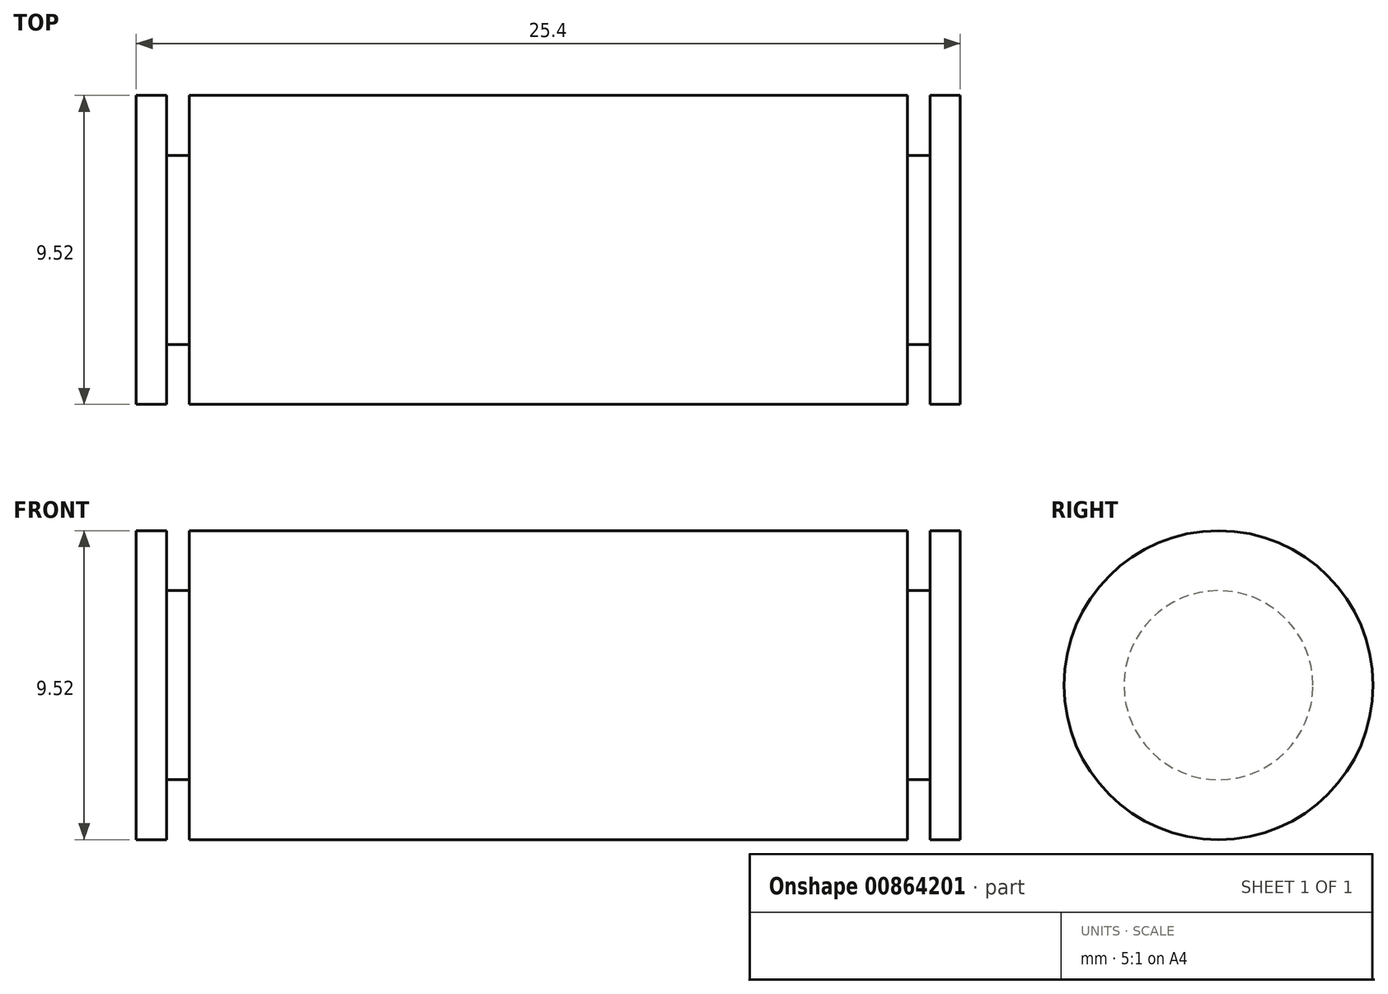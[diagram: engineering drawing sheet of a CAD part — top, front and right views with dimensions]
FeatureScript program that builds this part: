
annotation { "Feature Type Name" : "Feature", "Feature Type Description" : "" }
export const myFeature = defineFeature(function(context is Context, id is Id, definition is map)
    precondition{}
    {
        {
            var Q0;
            Q0=qCreatedBy(makeId("Right.planeOp"),FACE);
            var sketch = newSketch(context, id + "F0", { "sketchPlane" : qUnion([Q0])});
            skCircle(sketch, "E0", {"center": v(0, 0) * mm, "radius": 4.76 * mm});
            skSolve(sketch);
        }
        {
            var Q0;
            Q0=qSketchRegion(id+"F0",true);
            extrude(context, id + "F1", {"entities" : qUnion([Q0]), "depth" : 12.7 * mm, "offsetDistance" : 25.4 * mm});
        }
        {
            var Q0;
            Q0=qCreatedBy(makeId("Top.planeOp"),FACE);
            var sketch = newSketch(context, id + "F2", { "sketchPlane" : qUnion([Q0])});
            skLineSegment(sketch, "E1.bottom", {"start": v(11.77, 5.2) * mm, "end": v(11.07, 5.2) * mm});
            skLineSegment(sketch, "E1.top", {"start": v(11.77, 2.91) * mm, "end": v(11.07, 2.91) * mm});
            skLineSegment(sketch, "E1.left", {"start": v(11.77, 5.2) * mm, "end": v(11.77, 2.91) * mm});
            skLineSegment(sketch, "E1.right", {"start": v(11.07, 5.2) * mm, "end": v(11.07, 2.91) * mm});
            skLineSegment(sketch, "E2", {"start": v(15.49, 0) * mm, "end": v(7.73, 0) * mm, "construction": true});
            skSolve(sketch);
        }
        {
            var Q0;
            Q0=qSketchRegion(id+"F2",true);
            var Q1;
            Q1=sQuery(id+"F2.wireOp",EDGE,"E2");
            revolve(context, id + "F3", {"operationType" : NewBodyOperationType.REMOVE, "surfaceOperationType" : NewSurfaceOperationType.NEW, "entities" : qUnion([Q0]), "axis" : qUnion([Q1]), "revolveType" : RevolveType.FULL, "oppositeDirection" : true});
        }
        {
            var Q0;
            Q0=makeQuery(id+"F1.opExtrude","SWEPT_BODY",BODY,{"disambiguationData":[OSD([sQuery(id+"F0.wireOp",EDGE,"E0")])]});
            var Q1;
            Q1=qCreatedBy(makeId("Right.planeOp"),FACE);
            mirror(context, id + "F4", {"operationType" : NewBodyOperationType.ADD, "entities" : qUnion([Q0]), "mirrorPlane" : qUnion([Q1])});
        }
    });
